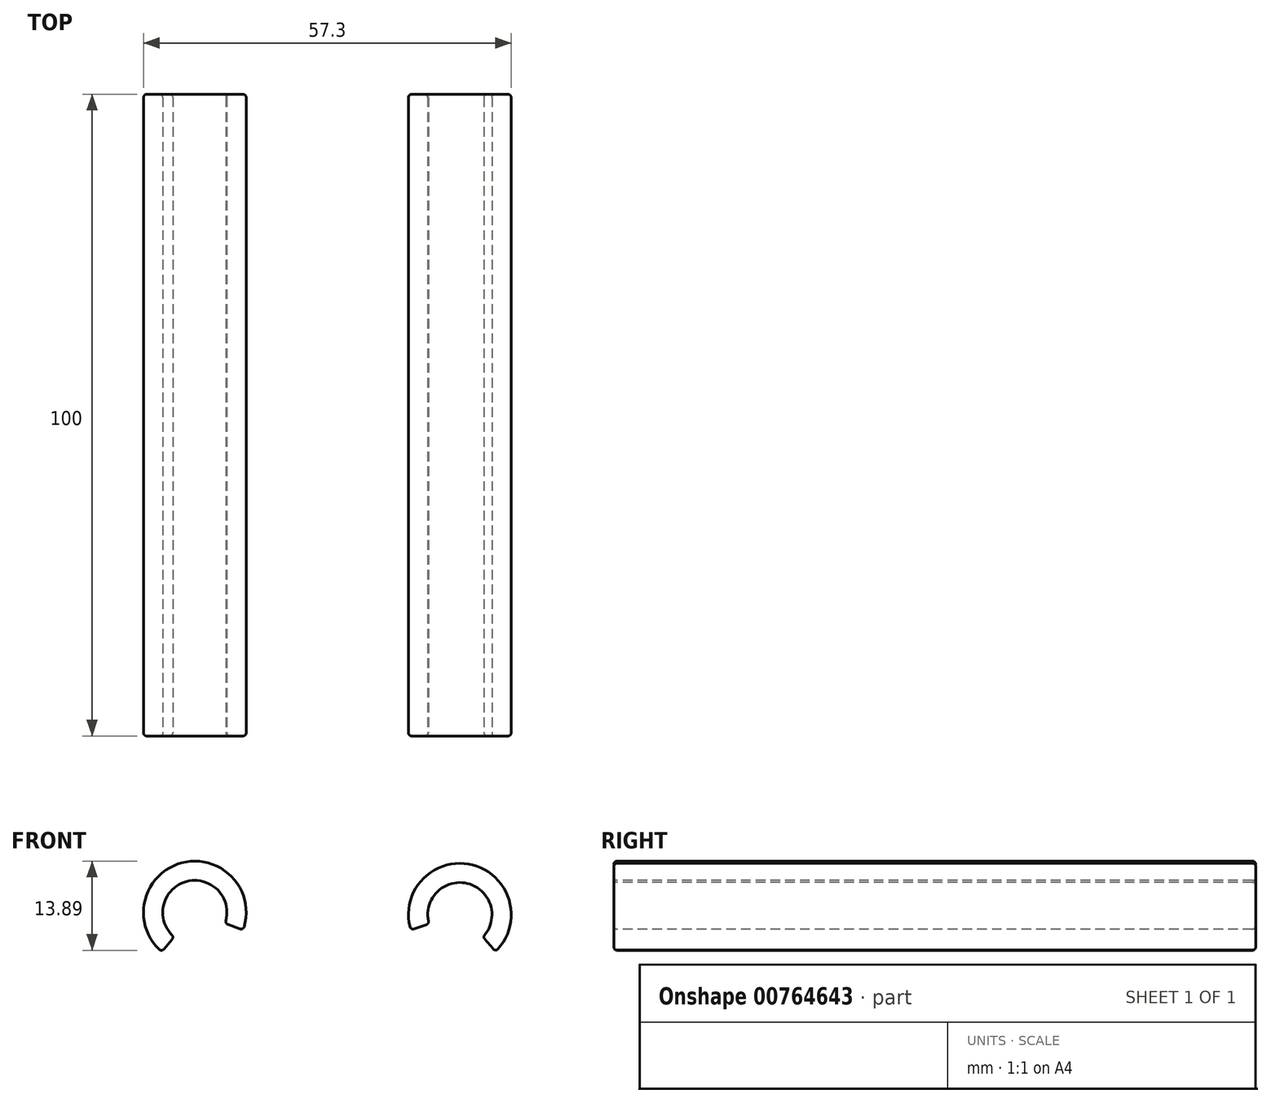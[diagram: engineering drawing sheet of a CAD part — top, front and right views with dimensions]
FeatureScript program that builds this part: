
annotation { "Feature Type Name" : "Feature", "Feature Type Description" : "" }
export const myFeature = defineFeature(function(context is Context, id is Id, definition is map)
    precondition{}
    {
        {
            var Q0;
            Q0=qCreatedBy(makeId("Front.planeOp"),FACE);
            var sketch = newSketch(context, id + "F0", { "sketchPlane" : qUnion([Q0])});
            skArc(sketch, "E0", {"start": v(-13.24, 35.99) * mm, "mid": v(-22.82, 46.45) * mm, "end": v(-25.92, 32.6) * mm});
            skArc(sketch, "E1", {"start": v(26.07, 32.6) * mm, "mid": v(22.53, 46.14) * mm, "end": v(12.9, 35.99) * mm});
            skLineSegment(sketch, "E2.top", {"start": v(36.1, 32.6) * mm, "end": v(26.07, 32.6) * mm});
            skLineSegment(sketch, "E2.left", {"start": v(36.1, 48.63) * mm, "end": v(36.1, 32.6) * mm});
            skLineSegment(sketch, "E2.right", {"start": v(-36.1, 48.63) * mm, "end": v(-36.1, 32.6) * mm});
            skPoint(sketch, "E2.middle", {"position": v(0, 40.62) * mm});
            skLineSegment(sketch, "E3.trimOffspring", {"start": v(-25.92, 32.6) * mm, "end": v(-36.1, 32.6) * mm});
            skLineSegment(sketch, "E4.left", {"start": v(11.12, 48.63) * mm, "end": v(11.12, 35.99) * mm});
            skLineSegment(sketch, "E4.right", {"start": v(-11.45, 48.63) * mm, "end": v(-11.45, 35.99) * mm});
            skLineSegment(sketch, "E5.top", {"start": v(-13.24, 35.99) * mm, "end": v(-11.45, 35.99) * mm});
            skLineSegment(sketch, "E6.trimOffspring", {"start": v(11.12, 35.99) * mm, "end": v(12.9, 35.99) * mm});
            skLineSegment(sketch, "E7.bottom", {"start": v(-11.45, 48.63) * mm, "end": v(11.12, 48.63) * mm});
            skLineSegment(sketch, "E7.top", {"start": v(-36.1, 51.35) * mm, "end": v(36.1, 51.35) * mm});
            skLineSegment(sketch, "E7.left", {"start": v(-36.1, 48.63) * mm, "end": v(-36.1, 51.35) * mm});
            skLineSegment(sketch, "E7.right", {"start": v(36.1, 48.63) * mm, "end": v(36.1, 51.35) * mm});
            skArc(sketch, "E8", {"start": v(-16.06, 37.02) * mm, "mid": v(-23.63, 42.8) * mm, "end": v(-20.76, 33.72) * mm});
            skArc(sketch, "E9", {"start": v(20.54, 33.39) * mm, "mid": v(23.53, 42.4) * mm, "end": v(15.74, 36.96) * mm});
            skLineSegment(sketch, "E10.bottom", {"start": v(-15.12, 35.67) * mm, "end": v(-0.3, 35.67) * mm});
            skLineSegment(sketch, "E10.top", {"start": v(-20.76, 31.28) * mm, "end": v(20.54, 31.28) * mm});
            skLineSegment(sketch, "E10.left", {"start": v(-20.76, 33.72) * mm, "end": v(-20.76, 31.28) * mm});
            skLineSegment(sketch, "E10.right", {"start": v(20.54, 33.39) * mm, "end": v(20.54, 31.28) * mm});
            skPoint(sketch, "E11.visualSharp", {"position": v(-16.79, 35.67) * mm});
            skArc(sketch, "E11.filletArc", {"start": v(-16.06, 37.02) * mm, "mid": v(-15.93, 36.1) * mm, "end": v(-15.12, 35.67) * mm});
            skPoint(sketch, "E12.visualSharp", {"position": v(16.34, 35.67) * mm});
            skArc(sketch, "E12.filletArc", {"start": v(14.79, 35.67) * mm, "mid": v(15.59, 36.08) * mm, "end": v(15.74, 36.96) * mm});
            skLineSegment(sketch, "E13", {"start": v(-0.3, 35.67) * mm, "end": v(-0.16, 35.54) * mm});
            skPoint(sketch, "E13.endSnap0", {"position": v(-0.16, 35.67) * mm});
            skLineSegment(sketch, "E14", {"start": v(-0.16, 35.54) * mm, "end": v(-0.03, 35.67) * mm});
            skLineSegment(sketch, "E15.trimOffspring", {"start": v(-0.03, 35.67) * mm, "end": v(14.79, 35.67) * mm});
            skLineSegment(sketch, "E16", {"start": v(-25.92, 32.6) * mm, "end": v(-22.95, 36.16) * mm});
            skLineSegment(sketch, "E17", {"start": v(26.07, 32.6) * mm, "end": v(22.91, 36.37) * mm});
            skLineSegment(sketch, "E18", {"start": v(12.9, 35.99) * mm, "end": v(15.74, 36.96) * mm});
            skLineSegment(sketch, "E19", {"start": v(-13.24, 35.99) * mm, "end": v(-16.06, 37.02) * mm});
            skSolve(sketch);
        }
        {
            var Q0;
            {var subQ0=sQuery(id+"F0.wireOp",EDGE,"E0");Q0=makeQuery(id+"F0.imprint","IMPRINT",FACE,{"disambiguationData":[TD([[makeQuery(id+"F0.imprint","IMPRINT",EDGE,{"derivedFrom":subQ0}),1.0]])]});}
            var Q1;
            {var subQ0=sQuery(id+"F0.wireOp",EDGE,"E1");Q1=makeQuery(id+"F0.imprint","IMPRINT",FACE,{"disambiguationData":[TD([[makeQuery(id+"F0.imprint","IMPRINT",EDGE,{"derivedFrom":subQ0}),1.0]])]});}
            extrude(context, id + "F1", {"entities" : qUnion([Q0, Q1]), "oppositeDirection" : true, "depth" : 100 * mm, "offsetDistance" : 25 * mm});
        }
        {
            var Q0;
            Q0=makeQuery(id+"F1.opExtrude","CAP_FACE",FACE,{"disambiguationData":[OSD([sQuery(id+"F0.wireOp",EDGE,"E0"),sQuery(id+"F0.wireOp",EDGE,"E8"),sQuery(id+"F0.wireOp",EDGE,"E16"),sQuery(id+"F0.wireOp",EDGE,"E19")])],"isStart":true});
            var Q1;
            Q1=makeQuery(id+"F1.opExtrude","CAP_FACE",FACE,{"disambiguationData":[OSD([sQuery(id+"F0.wireOp",EDGE,"E1"),sQuery(id+"F0.wireOp",EDGE,"E9"),sQuery(id+"F0.wireOp",EDGE,"E17"),sQuery(id+"F0.wireOp",EDGE,"E18")])],"isStart":true});
            var Q2;
            Q2=makeQuery(id+"F1.opExtrude","CAP_FACE",FACE,{"disambiguationData":[OSD([sQuery(id+"F0.wireOp",EDGE,"E1"),sQuery(id+"F0.wireOp",EDGE,"E9"),sQuery(id+"F0.wireOp",EDGE,"E17"),sQuery(id+"F0.wireOp",EDGE,"E18")])],"isStart":false});
            var Q3;
            Q3=makeQuery(id+"F1.opExtrude","CAP_FACE",FACE,{"disambiguationData":[OSD([sQuery(id+"F0.wireOp",EDGE,"E0"),sQuery(id+"F0.wireOp",EDGE,"E8"),sQuery(id+"F0.wireOp",EDGE,"E16"),sQuery(id+"F0.wireOp",EDGE,"E19")])],"isStart":false});
            var Q4;
            Q4=makeQuery(id+"F1.opExtrude","SWEPT_FACE",FACE,{"disambiguationData":[OSD([sQuery(id+"F0.wireOp",EDGE,"E16")])]});
            var Q5;
            Q5=makeQuery(id+"F1.opExtrude","SWEPT_FACE",FACE,{"disambiguationData":[OSD([sQuery(id+"F0.wireOp",EDGE,"E19")])]});
            var Q6;
            Q6=makeQuery(id+"F1.opExtrude","SWEPT_EDGE",EDGE,{"disambiguationData":[OSD([sQuery(id+"F0.wireOp",EDGE,"E1"),sQuery(id+"F0.wireOp",EDGE,"E6.trimOffspring"),sQuery(id+"F0.wireOp",EDGE,"E18")])]});
            var Q7;
            Q7=makeQuery(id+"F1.opExtrude","SWEPT_EDGE",EDGE,{"disambiguationData":[OSD([sQuery(id+"F0.wireOp",EDGE,"E9"),sQuery(id+"F0.wireOp",EDGE,"E12.filletArc"),sQuery(id+"F0.wireOp",EDGE,"E18")])]});
            var Q8;
            Q8=makeQuery(id+"F1.opExtrude","SWEPT_FACE",FACE,{"disambiguationData":[OSD([sQuery(id+"F0.wireOp",EDGE,"E17")])]});
            fillet(context, id + "F2", {"entities" : qUnion([Q0, Q1, Q2, Q3, Q4, Q5, Q6, Q7, Q8]), "radius" : 0.5 * mm, "tangentPropagation" : true, "allowEdgeOverflow" : false});
        }
    });
